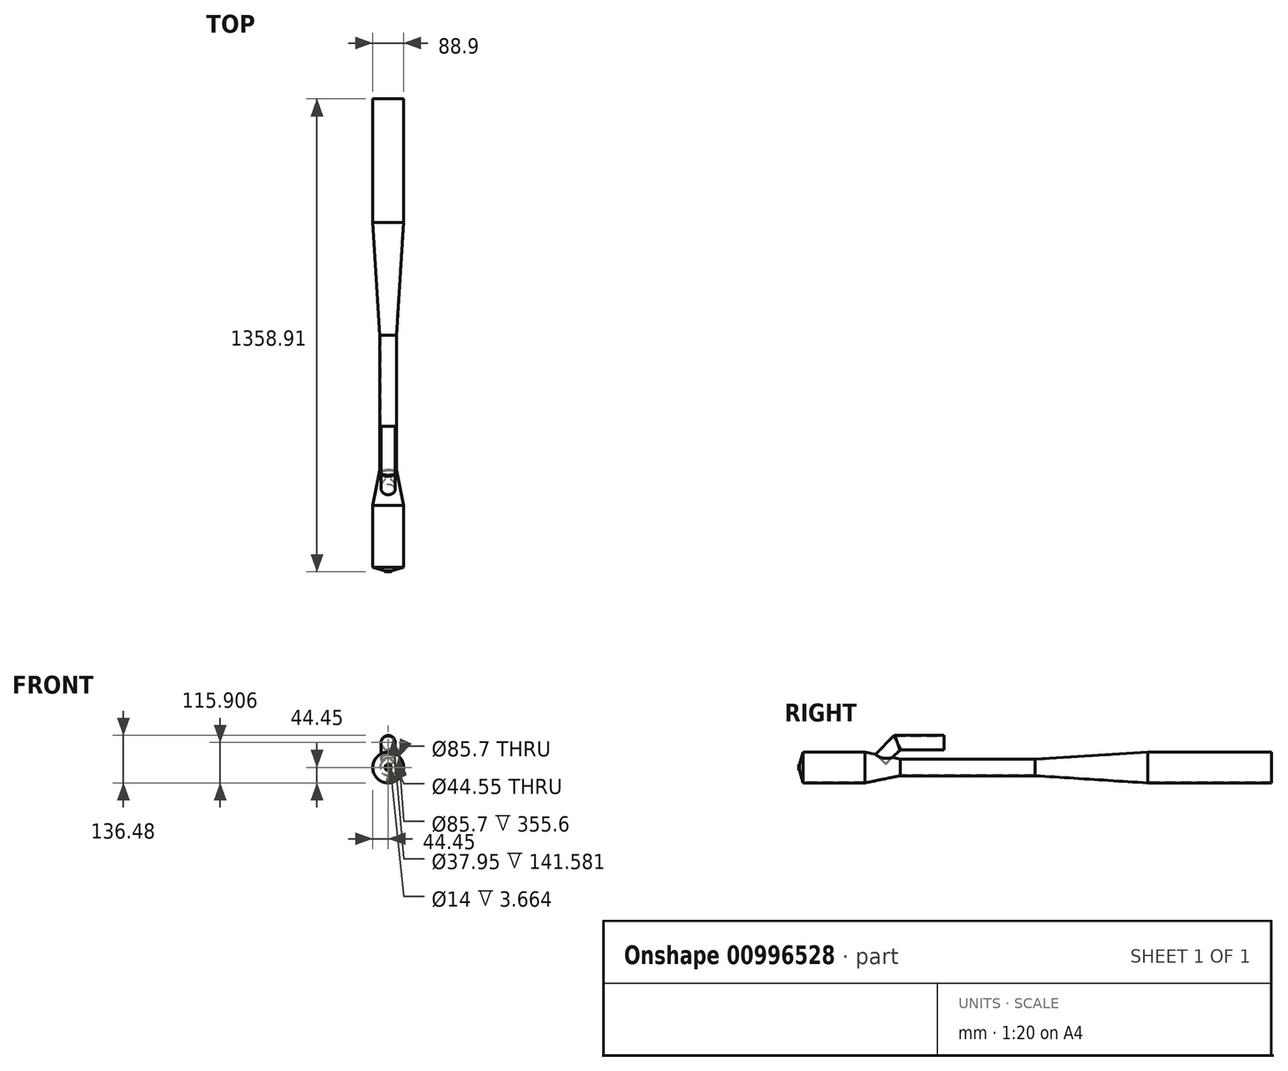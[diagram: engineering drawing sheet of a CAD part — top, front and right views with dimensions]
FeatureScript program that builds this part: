
annotation { "Feature Type Name" : "Feature", "Feature Type Description" : "" }
export const myFeature = defineFeature(function(context is Context, id is Id, definition is map)
    precondition{}
    {
        {
            var Q0;
            Q0=qCreatedBy(makeId("Right.planeOp"),FACE);
            var sketch = newSketch(context, id + "F0", { "sketchPlane" : qUnion([Q0])});
            skLineSegment(sketch, "E0.bottom", {"start": v(-682.62, 0) * mm, "end": v(682.62, 0) * mm, "construction": true});
            skLineSegment(sketch, "E0.top", {"start": v(-682.62, 44.45) * mm, "end": v(-676.28, 44.45) * mm});
            skLineSegment(sketch, "E0.left", {"start": v(-682.62, 0) * mm, "end": v(-682.62, 44.45) * mm});
            skLineSegment(sketch, "E0.right", {"start": v(682.62, 0) * mm, "end": v(682.62, 44.45) * mm});
            skLineSegment(sketch, "E1", {"start": v(-682.62, 0) * mm, "end": v(682.62, 0) * mm});
            skLineSegment(sketch, "E2.bottom", {"start": v(-682.62, 0) * mm, "end": v(-663.58, 0) * mm});
            skLineSegment(sketch, "E2.right", {"start": v(-663.58, 0) * mm, "end": v(-663.58, 44.45) * mm});
            skLineSegment(sketch, "E3.bottom", {"start": v(-663.58, 0) * mm, "end": v(-485.78, 0) * mm});
            skLineSegment(sketch, "E3.top", {"start": v(-663.58, 44.45) * mm, "end": v(-485.78, 44.45) * mm});
            skLineSegment(sketch, "E3.right", {"start": v(-485.78, 0) * mm, "end": v(-485.78, 44.45) * mm});
            skLineSegment(sketch, "E4.top", {"start": v(-485.78, 0) * mm, "end": v(-384.18, 0) * mm});
            skLineSegment(sketch, "E4.left", {"start": v(-485.78, 44.45) * mm, "end": v(-485.78, 0) * mm});
            skLineSegment(sketch, "E4.right", {"start": v(-384.18, 23.88) * mm, "end": v(-384.18, 0) * mm});
            skLineSegment(sketch, "E5.top", {"start": v(-384.18, 0) * mm, "end": v(3.18, 0) * mm});
            skLineSegment(sketch, "E5.right", {"start": v(3.18, 23.88) * mm, "end": v(3.18, 0) * mm});
            skLineSegment(sketch, "E6.top", {"start": v(3.18, 0) * mm, "end": v(327.03, 0) * mm});
            skLineSegment(sketch, "E6.right", {"start": v(327.03, 44.45) * mm, "end": v(327.03, 0) * mm});
            skLineSegment(sketch, "E7.bottom", {"start": v(327.03, 0) * mm, "end": v(682.62, 0) * mm});
            skLineSegment(sketch, "E7.top", {"start": v(327.03, 44.45) * mm, "end": v(682.62, 44.45) * mm});
            skLineSegment(sketch, "E7.left", {"start": v(327.03, 0) * mm, "end": v(327.03, 44.45) * mm});
            skLineSegment(sketch, "E8", {"start": v(-384.18, 23.88) * mm, "end": v(3.18, 23.88) * mm});
            skLineSegment(sketch, "E9", {"start": v(-384.18, 23.88) * mm, "end": v(-485.78, 44.45) * mm});
            skLineSegment(sketch, "E10", {"start": v(3.17, 23.88) * mm, "end": v(327.03, 44.45) * mm});
            skLineSegment(sketch, "E11", {"start": v(-676.28, 44.45) * mm, "end": v(-676.28, 0) * mm});
            skLineSegment(sketch, "E12", {"start": v(-676.28, 0) * mm, "end": v(-663.58, 44.45) * mm});
            skLineSegment(sketch, "E13", {"start": v(-454.66, 38.15) * mm, "end": v(-412.83, 79.98) * mm});
            skLineSegment(sketch, "E14", {"start": v(-412.83, 79.98) * mm, "end": v(-383.73, 50.88) * mm});
            skLineSegment(sketch, "E15", {"start": v(-383.73, 50.88) * mm, "end": v(-406.26, 28.35) * mm});
            skLineSegment(sketch, "E16", {"start": v(-383.73, 50.88) * mm, "end": v(-258.54, 50.88) * mm});
            skLineSegment(sketch, "E17", {"start": v(-258.54, 50.88) * mm, "end": v(-258.54, 92.03) * mm});
            skLineSegment(sketch, "E18", {"start": v(-258.54, 92.03) * mm, "end": v(-400.78, 92.03) * mm});
            skLineSegment(sketch, "E19", {"start": v(-412.83, 79.98) * mm, "end": v(-400.78, 92.03) * mm});
            skLineSegment(sketch, "E20", {"start": v(-400.78, 92.03) * mm, "end": v(-383.73, 50.88) * mm});
            skLineSegment(sketch, "E21", {"start": v(-400.78, 92.03) * mm, "end": v(-417.15, 92.03) * mm});
            skLineSegment(sketch, "E22", {"start": v(-400.78, 92.03) * mm, "end": v(-407.24, 107.64) * mm});
            skLineSegment(sketch, "E23", {"start": v(-398.28, 65.43) * mm, "end": v(-430.46, 33.25) * mm, "construction": true});
            skLineSegment(sketch, "E24", {"start": v(-258.54, 71.46) * mm, "end": v(-392.25, 71.46) * mm, "construction": true});
            skLineSegment(sketch, "E25", {"start": v(-398.28, 65.43) * mm, "end": v(-392.25, 71.46) * mm, "construction": true});
            skLineSegment(sketch, "E26", {"start": v(-674.61, 0) * mm, "end": v(-662.37, 42.85) * mm});
            skLineSegment(sketch, "E27", {"start": v(-662.37, 42.85) * mm, "end": v(-485.78, 42.85) * mm});
            skLineSegment(sketch, "E28", {"start": v(-485.78, 42.85) * mm, "end": v(-384.18, 22.28) * mm});
            skLineSegment(sketch, "E29", {"start": v(-384.18, 22.28) * mm, "end": v(3.18, 22.28) * mm});
            skLineSegment(sketch, "E30", {"start": v(3.18, 22.28) * mm, "end": v(327.03, 42.85) * mm});
            skLineSegment(sketch, "E31", {"start": v(327.03, 42.85) * mm, "end": v(682.62, 42.85) * mm});
            skLineSegment(sketch, "E32", {"start": v(-432.34, 33.63) * mm, "end": v(-392.92, 73.06) * mm});
            skLineSegment(sketch, "E33", {"start": v(-392.92, 73.06) * mm, "end": v(-258.54, 73.06) * mm});
            skLineSegment(sketch, "E34", {"start": v(-258.54, 90.43) * mm, "end": v(-400.11, 90.43) * mm});
            skLineSegment(sketch, "E35", {"start": v(-400.11, 90.43) * mm, "end": v(-452.77, 37.77) * mm});
            skLineSegment(sketch, "E36.MirrorCS", {"start": v(-258.54, 52.48) * mm, "end": v(-400.11, 52.48) * mm});
            skLineSegment(sketch, "E37.MirrorCS", {"start": v(-373.28, 63.6) * mm, "end": v(-425.94, 10.93) * mm});
            skSolve(sketch);
        }
        {
            var Q0;
            {var subQ1=sQuery(id+"F0.wireOp",EDGE,"E3.top");Q0=makeQuery(id+"F0.imprint","IMPRINT",FACE,{"disambiguationData":[TD([[makeQuery(id+"F0.imprint","IMPRINT",EDGE,{"derivedFrom":subQ1}),-1.0]])]});}
            var Q1;
            {var subQ3=sQuery(id+"F0.wireOp",EDGE,"E12");Q1=makeQuery(id+"F0.imprint","IMPRINT",FACE,{"disambiguationData":[TD([[makeQuery(id+"F0.imprint","IMPRINT",EDGE,{"derivedFrom":subQ3}),-1.0]])]});}
            var Q2;
            {var subQ5=sQuery(id+"F0.wireOp",EDGE,"E9");var subQ6=makeQuery(id+"F0.imprint","INTERSECT",VERTEX,{"derivedFrom":[subQ5,sQuery(id+"F0.wireOp",EDGE,"E15")]});Q2=makeQuery(id+"F0.imprint","IMPRINT",FACE,{"disambiguationData":[TD([[makeQuery(id+"F0.imprint","IMPRINT",EDGE,{"disambiguationData":[TD([[subQ6,-1.0]])],"derivedFrom":subQ5}),1.0]])]});}
            var Q3;
            {var subQ2=sQuery(id+"F0.wireOp",EDGE,"E8");Q3=makeQuery(id+"F0.imprint","IMPRINT",FACE,{"disambiguationData":[TD([[makeQuery(id+"F0.imprint","IMPRINT",EDGE,{"derivedFrom":subQ2}),-1.0]])]});}
            var Q4;
            {var subQ2=sQuery(id+"F0.wireOp",EDGE,"E10");Q4=makeQuery(id+"F0.imprint","IMPRINT",FACE,{"disambiguationData":[TD([[makeQuery(id+"F0.imprint","IMPRINT",EDGE,{"derivedFrom":subQ2}),-1.0]])]});}
            var Q5;
            {var subQ0=sQuery(id+"F0.wireOp",EDGE,"E7.top");Q5=makeQuery(id+"F0.imprint","IMPRINT",FACE,{"disambiguationData":[TD([[makeQuery(id+"F0.imprint","IMPRINT",EDGE,{"derivedFrom":subQ0}),-1.0]])]});}
            var Q6;
            {var subQ0=sQuery(id+"F0.wireOp",EDGE,"E9");var subQ1=makeQuery(id+"F0.imprint","INTERSECT",VERTEX,{"derivedFrom":[subQ0,sQuery(id+"F0.wireOp",EDGE,"E32")]});Q6=makeQuery(id+"F0.imprint","IMPRINT",FACE,{"disambiguationData":[TD([[makeQuery(id+"F0.imprint","IMPRINT",EDGE,{"disambiguationData":[TD([[subQ1,1.0]])],"derivedFrom":subQ0}),1.0]])]});}
            var Q7;
            Q7=sQuery(id+"F0.wireOp",EDGE,"E3.bottom");
            revolve(context, id + "F1", {"surfaceOperationType" : NewSurfaceOperationType.NEW, "entities" : qUnion([Q0, Q1, Q2, Q3, Q4, Q5, Q6]), "axis" : qUnion([Q7]), "revolveType" : RevolveType.FULL});
        }
        {
            var Q0;
            {var subQ0=sQuery(id+"F0.wireOp",EDGE,"E13");Q0=makeQuery(id+"F0.imprint","IMPRINT",FACE,{"disambiguationData":[TD([[makeQuery(id+"F0.imprint","IMPRINT",EDGE,{"derivedFrom":subQ0}),-1.0]])]});}
            var Q1;
            Q1=sQuery(id+"F0.wireOp",EDGE,"E23");
            revolve(context, id + "F2", {"operationType" : NewBodyOperationType.ADD, "surfaceOperationType" : NewSurfaceOperationType.NEW, "entities" : qUnion([Q0]), "axis" : qUnion([Q1]), "revolveType" : RevolveType.FULL});
        }
        {
            var Q0;
            Q0=makeQuery(id+"F2.opRevolve","SWEPT_FACE",FACE,{"disambiguationData":[OSD([sQuery(id+"F0.wireOp",EDGE,"E14")])]});
            var sketch = newSketch(context, id + "F3", { "sketchPlane" : qUnion([Q0])});
            skCircle(sketch, "E38.0", {"center": v(0, 327.9) * mm, "radius": 18.97 * mm});
            skCircle(sketch, "E39.0", {"center": v(0, 327.9) * mm, "radius": 20.57 * mm});
            skSolve(sketch);
        }
        {
            var Q0;
            Q0=makeQuery(id+"F3.imprint","IMPRINT",FACE,{"disambiguationData":[TD([[makeQuery(id+"F3.imprint","IMPRINT",EDGE,{"derivedFrom":sQuery(id+"F3.wireOp",EDGE,"E38.0")}),1.0]])]});
            extrude(context, id + "F4", {"entities" : qUnion([Q0]), "operationType" : NewBodyOperationType.REMOVE, "oppositeDirection" : true, "depth" : 70 * mm, "offsetDistance" : 25 * mm});
        }
        {
            var Q0;
            {var subQ0=sQuery(id+"F0.wireOp",EDGE,"E37.MirrorCS");var subQ1=sQuery(id+"F0.wireOp",EDGE,"E14");var subQ2=makeQuery(id+"F0.imprint","INTERSECT",VERTEX,{"derivedFrom":[subQ1,subQ0]});Q0=makeQuery(id+"F0.imprint","IMPRINT",FACE,{"disambiguationData":[TD([[makeQuery(id+"F0.imprint","IMPRINT",EDGE,{"disambiguationData":[TD([[subQ2,1.0]])],"derivedFrom":subQ0}),1.0]])]});}
            var Q1;
            Q1=sQuery(id+"F0.wireOp",EDGE,"E25");
            revolve(context, id + "F5", {"operationType" : NewBodyOperationType.ADD, "surfaceOperationType" : NewSurfaceOperationType.NEW, "entities" : qUnion([Q0]), "axis" : qUnion([Q1]), "revolveType" : RevolveType.FULL});
        }
        {
            var Q0;
            Q0=qCreatedBy(makeId("Front.planeOp"),FACE);
            var Q1;
            Q1=sQuery(id+"F0.wireOp",VERTEX,"E16.end");
            cPlane(context, id + "F6", {"entities" : qUnion([Q0, Q1]), "cplaneType" : CPlaneType.PLANE_POINT, "offset" : 25 * mm, "width" : 150 * mm, "height" : 150 * mm});
        }
        {
            var Q0;
            Q0=makeQuery(id+"F3.imprint","IMPRINT",FACE,{"disambiguationData":[TD([[makeQuery(id+"F3.imprint","IMPRINT",EDGE,{"derivedFrom":sQuery(id+"F3.wireOp",EDGE,"E38.0")}),-1.0]])]});
            var Q1;
            Q1=sQuery(id+"F0.wireOp",EDGE,"E35");
            var Q2;
            Q2=sQuery(id+"F0.wireOp",EDGE,"E34");
            sweep(context, id + "F7", {"operationType" : NewBodyOperationType.ADD, "profiles" : qUnion([Q0]), "path" : qUnion([Q1, Q2])});
        }
        {
            var Q0;
            Q0=makeQuery(id+"F7.opSweep","MID_CAP_EDGE",EDGE,{"disambiguationData":[OSD([sQuery(id+"F0.wireOp",VERTEX,"E34.end"),sQuery(id+"F3.wireOp",EDGE,"E39.0")])],"capPos":1.0});
            fillet(context, id + "F8", {"entities" : qUnion([Q0]), "radius" : 5 * mm, "tangentPropagation" : true, "allowEdgeOverflow" : false});
        }
        {
            var Q0;
            Q0=qCreatedBy(makeId("Front.planeOp"),FACE);
            var Q1;
            Q1=makeQuery(id+"F1.opRevolve","SWEPT_VERTEX",VERTEX,{"disambiguationData":[OSD([sQuery(id+"F0.wireOp",EDGE,"E1"),sQuery(id+"F0.wireOp",EDGE,"E11"),sQuery(id+"F0.wireOp",EDGE,"E12")])]});
            cPlane(context, id + "F9", {"entities" : qUnion([Q0, Q1]), "cplaneType" : CPlaneType.PLANE_POINT, "offset" : 25 * mm, "width" : 150 * mm, "height" : 150 * mm});
        }
        {
            var Q0;
            Q0=qCreatedBy(id+"F9.planeOp",FACE);
            var sketch = newSketch(context, id + "F10", { "sketchPlane" : qUnion([Q0])});
            skCircle(sketch, "E40.cCircle", {"center": v(0, 0) * mm, "radius": 8.5 * mm, "construction": true});
            skLineSegment(sketch, "E40.0", {"start": v(4.9, -8.5) * mm, "end": v(-4.9, -8.5) * mm});
            skLineSegment(sketch, "E40.1", {"start": v(-4.9, -8.5) * mm, "end": v(-9.81, 0) * mm});
            skLineSegment(sketch, "E40.2", {"start": v(-9.81, 0) * mm, "end": v(-4.9, 8.5) * mm});
            skLineSegment(sketch, "E40.3", {"start": v(-4.9, 8.5) * mm, "end": v(4.9, 8.5) * mm});
            skLineSegment(sketch, "E40.4", {"start": v(4.9, 8.5) * mm, "end": v(9.81, 0) * mm});
            skLineSegment(sketch, "E40.5", {"start": v(9.81, 0) * mm, "end": v(4.9, -8.5) * mm});
            skPoint(sketch, "E40.0.midPoint", {"position": v(0, -8.5) * mm});
            skCircle(sketch, "E41", {"center": v(0, 0) * mm, "radius": 7 * mm});
            skSolve(sketch);
        }
        {
            var Q0;
            Q0=makeQuery(id+"F10.imprint","IMPRINT",FACE,{"disambiguationData":[TD([[makeQuery(id+"F10.imprint","IMPRINT",EDGE,{"derivedFrom":sQuery(id+"F10.wireOp",EDGE,"E41")}),1.0]])]});
            extrude(context, id + "F11", {"entities" : qUnion([Q0]), "operationType" : NewBodyOperationType.REMOVE, "oppositeDirection" : true, "depth" : 25 * mm, "offsetDistance" : 25 * mm});
        }
        {
            var Q0;
            Q0=makeQuery(id+"F10.imprint","IMPRINT",FACE,{"disambiguationData":[TD([[makeQuery(id+"F10.imprint","IMPRINT",EDGE,{"derivedFrom":sQuery(id+"F10.wireOp",EDGE,"E40.0")}),-1.0]])]});
            extrude(context, id + "F12", {"entities" : qUnion([Q0]), "operationType" : NewBodyOperationType.ADD, "endBound" : BoundingType.UP_TO_NEXT, "oppositeDirection" : true, "depth" : 25 * mm, "offsetDistance" : 25 * mm});
        }
    });
